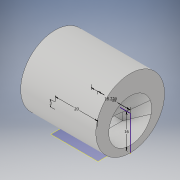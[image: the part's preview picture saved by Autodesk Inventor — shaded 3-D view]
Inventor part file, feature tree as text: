
AUTODESK INVENTOR PART (.ipt)
format: ipt  version: 2019 (Build 230136000, 136)  size: 232,960 bytes
history: native  units: in
note: dims shown in document units (in); Inventor stores cm internally (conversion verified against a paired STEP export)
features: sketch x7, extrude x2, revolve x1, loft x1, fillet x1, plane x1, other x1
ambient origin geometry x8: Origin, YZ Plane, XZ Plane, XY Plane, X Axis, Y Axis, Z Axis, Center Point
bodies: Solid1 (feature_tree)
feature tree (14):
  revolve  "Revolution1"  [1 undecoded]
  sketch  "Sketch2"  dims[d3=0.5906in d4=90.0deg]
  extrude  "Extrusion1"  TaperAngle=90.0deg  [1 undecoded]
  sketch  "Sketch4"  dims[d9=0.7874in d10=0.0in d11=90.0deg]
  sketch  "Sketch5"  dims[d12=0.0in d13=90.0deg]
  loft  "Loft1"
  fillet  "Fillet1"  Radius=0.1969in
  sketch  "Sketch6"  dims[d14=0.2362in]
  plane  "Work Plane1"
  extrude  "Extrusion2"  TaperAngle=0.0deg  [1 undecoded]
  sketch  "Sketch1"  dims[d0=0.1181in d1=0.7874in]
  sketch  "Sketch3"  dims[d5=0.1181in d6=0.5118in d7=0.1969in d8=0.0in]
  other  "Edges1"
  sketch  "Sketch7"  dims[d15=0.5118in d16=0.1969in d17=0.0in d18=0.6299in d19=0.7177in]
note: 3 required parameter values undecoded (feature->parameter linkage not recoverable at this tier; creation-order binding heuristic only, values carry confidence <= 0.55)